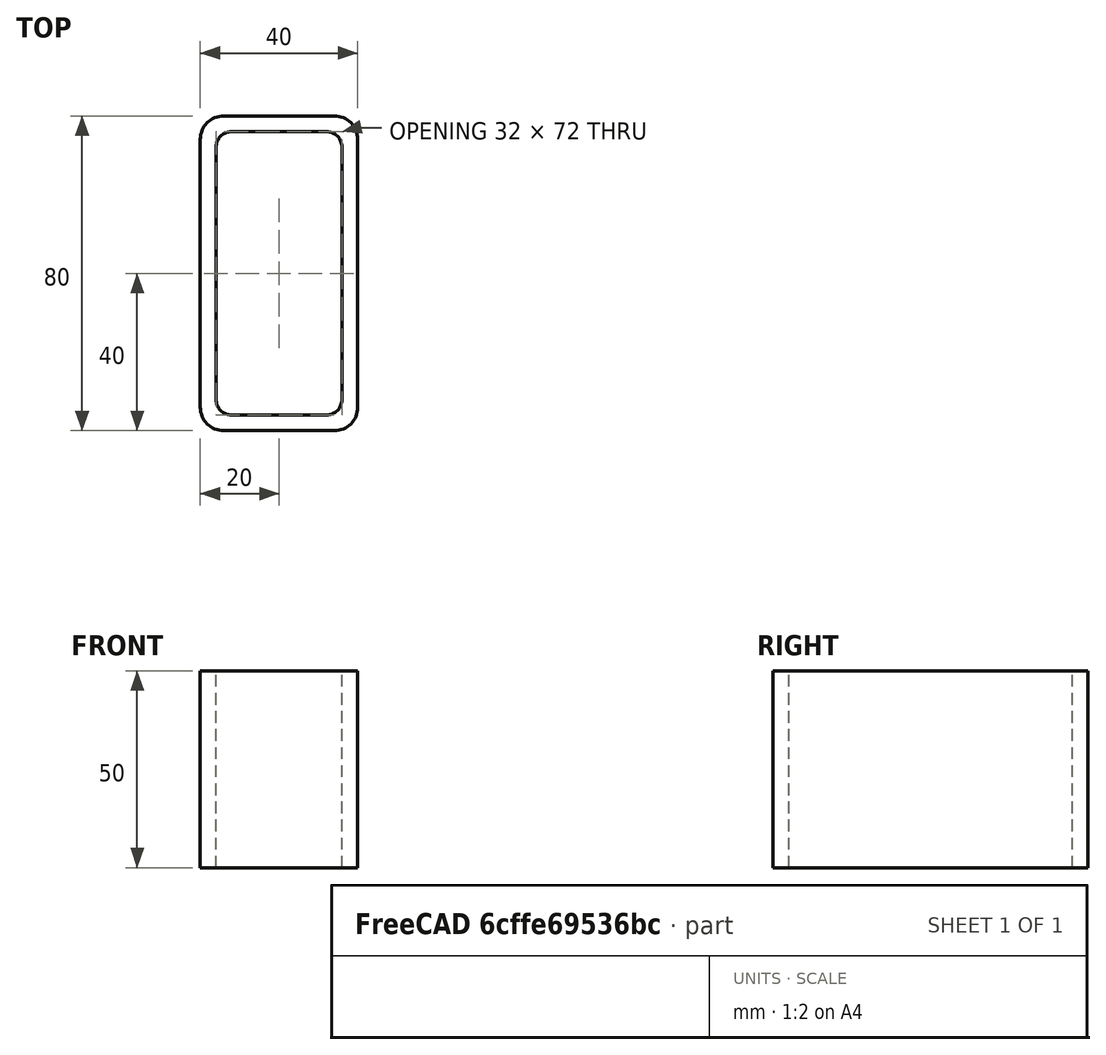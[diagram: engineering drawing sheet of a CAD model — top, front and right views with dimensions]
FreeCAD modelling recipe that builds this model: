
FCSTD DOCUMENT  (FreeCAD 0.15R4671 (Git))
Label: Rectangular hollow section 80x40x4 EN10219 S235JRH
License: All rights reserved
LicenseURL: http://en.wikipedia.org/wiki/All_rights_reserved
objects: Sketcher::SketchObject×1, Part::Extrusion×1
note: 2 computed .brp shape members not serialized (recipe doc carries the construction recipe); baked Part::Feature solids carry a one-line shape summary decoded from their .brp

FEATURE [Sketcher::SketchObject] Sketch
  sketch-geometry (16):
    g0: LineSegment StartX=-12 StartY=36 StartZ=0 EndX=12 EndY=36 EndZ=0
    g1: LineSegment StartX=16 StartY=32 StartZ=0 EndX=16 EndY=-32 EndZ=0
    g2: LineSegment StartX=12 StartY=-36 StartZ=0 EndX=-12 EndY=-36 EndZ=0
    g3: LineSegment StartX=-16 StartY=-32 StartZ=0 EndX=-16 EndY=32 EndZ=0
    g4: LineSegment StartX=-14 StartY=40 StartZ=0 EndX=14 EndY=40 EndZ=0
    g5: LineSegment StartX=20 StartY=34 StartZ=0 EndX=20 EndY=-34 EndZ=0
    g6: LineSegment StartX=14 StartY=-40 StartZ=0 EndX=-14 EndY=-40 EndZ=0
    g7: LineSegment StartX=-20 StartY=-34 StartZ=0 EndX=-20 EndY=34 EndZ=0
    g8: ArcOfCircle CenterX=-12 CenterY=32 CenterZ=0 NormalX=0 NormalY=0 NormalZ=1 Radius=4 StartAngle=1.5708 EndAngle=3.14159
    g9: ArcOfCircle CenterX=12 CenterY=32 CenterZ=0 NormalX=0 NormalY=0 NormalZ=1 Radius=4 StartAngle=0 EndAngle=1.5708
    g10: ArcOfCircle CenterX=12 CenterY=-32 CenterZ=0 NormalX=0 NormalY=0 NormalZ=1 Radius=4 StartAngle=4.71239 EndAngle=6.28319
    g11: ArcOfCircle CenterX=-12 CenterY=-32 CenterZ=0 NormalX=0 NormalY=0 NormalZ=1 Radius=4 StartAngle=3.14159 EndAngle=4.71239
    g12: ArcOfCircle CenterX=14 CenterY=34 CenterZ=0 NormalX=0 NormalY=0 NormalZ=1 Radius=6 StartAngle=0 EndAngle=1.5708
    g13: ArcOfCircle CenterX=14 CenterY=-34 CenterZ=0 NormalX=0 NormalY=0 NormalZ=1 Radius=6 StartAngle=4.71239 EndAngle=6.28319
    g14: ArcOfCircle CenterX=-14 CenterY=-34 CenterZ=0 NormalX=0 NormalY=0 NormalZ=1 Radius=6 StartAngle=3.14159 EndAngle=4.71239
    g15: ArcOfCircle CenterX=-14 CenterY=34 CenterZ=0 NormalX=0 NormalY=0 NormalZ=1 Radius=6 StartAngle=1.5708 EndAngle=3.14159
  constraints (36):
    c: Horizontal(g2)
    c: Vertical(g3)
    c: Horizontal(g6)
    c: Vertical(g7)
    c: Tangent(g3,g8) = 1.5708
    c: Tangent(g0,g8) = 1.5708
    c: Tangent(g0,g9) = 1.5708
    c: Tangent(g1,g9) = 1.5708
    c: Tangent(g1,g10) = 1.5708
    c: Tangent(g2,g10) = 1.5708
    c: Tangent(g2,g11) = 1.5708
    c: Tangent(g3,g11) = 1.5708
    c: Tangent(g4,g12) = 1.5708
    c: Tangent(g5,g12) = 1.5708
    c: Tangent(g5,g13) = 1.5708
    c: Tangent(g6,g13) = 1.5708
    c: Tangent(g6,g14) = 1.5708
    c: Tangent(g7,g14) = 1.5708
    c: Tangent(g7,g15) = 1.5708
    c: Tangent(g4,g15) = 1.5708
    c: Equal(g9,g8)
    c: Equal(g9,g11)
    c: Equal(g9,g10)
    c: Equal(g12,g15)
    c: Equal(g12,g14)
    c: Equal(g12,g13)
    c: Symmetric(g4,g6,g-1)
    c: Symmetric(g7,g5,g-2)
    c: DistanceY(g4,g6) = -80
    c: DistanceX(g7,g5) = 40
    c: Symmetric(g3,g1,g-2)
    c: Symmetric(g0,g2,g-1)
    c: DistanceY(g0,g4) = 4
    c: DistanceX(g5,g1) = -4
    c: Radius(g9) = 4
    c: Radius(g12) = 6
FEATURE [Part::Extrusion] Extrude  label="Rectangular hollow section 80x40x4 EN10219 S235JRH"
  Base = -> Sketch
  Dir = (0,0,50)
  Solid = true
